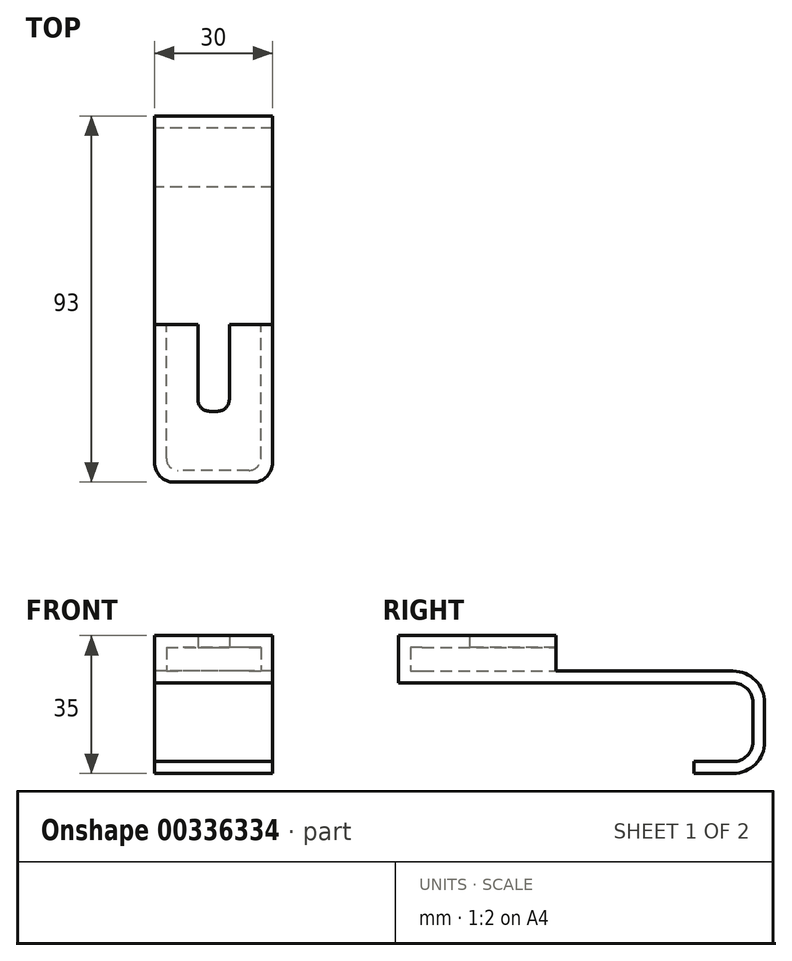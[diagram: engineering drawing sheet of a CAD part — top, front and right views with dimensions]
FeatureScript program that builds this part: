
annotation { "Feature Type Name" : "Feature", "Feature Type Description" : "" }
export const myFeature = defineFeature(function(context is Context, id is Id, definition is map)
    precondition{}
    {
        {
            var Q0;
            Q0=qCreatedBy(makeId("Top.planeOp"),FACE);
            var sketch = newSketch(context, id + "F0", { "sketchPlane" : qUnion([Q0])});
            skLineSegment(sketch, "E0.bottom", {"start": v(-5, 0) * mm, "end": v(-25, 0) * mm});
            skLineSegment(sketch, "E0.top", {"start": v(0, 40) * mm, "end": v(-30, 40) * mm});
            skLineSegment(sketch, "E0.left", {"start": v(0, 5) * mm, "end": v(0, 40) * mm});
            skLineSegment(sketch, "E0.right", {"start": v(-30, 5) * mm, "end": v(-30, 40) * mm});
            skPoint(sketch, "E1.visualSharp", {"position": v(-30, 0) * mm});
            skArc(sketch, "E1.filletArc", {"start": v(-30, 5) * mm, "mid": v(-28.54, 1.46) * mm, "end": v(-25, 0) * mm});
            skPoint(sketch, "E2.visualSharp", {"position": v(0, 0) * mm});
            skArc(sketch, "E2.filletArc", {"start": v(-5, 0) * mm, "mid": v(-1.46, 1.46) * mm, "end": v(0, 5) * mm});
            skSolve(sketch);
        }
        {
            var Q0;
            Q0=makeQuery(id+"F0.imprint","IMPRINT",FACE,{"disambiguationData":[TD([[makeQuery(id+"F0.imprint","IMPRINT",EDGE,{"derivedFrom":sQuery(id+"F0.wireOp",EDGE,"E0.bottom")}),-1.0]])]});
            extrude(context, id + "F1", {"entities" : qUnion([Q0]), "depth" : 3 * mm});
        }
        {
            var Q0;
            Q0=makeQuery(id+"F1.opExtrude","CAP_FACE",FACE,{"disambiguationData":[OSD([sQuery(id+"F0.wireOp",EDGE,"E0.bottom"),sQuery(id+"F0.wireOp",EDGE,"E0.top"),sQuery(id+"F0.wireOp",EDGE,"E0.left"),sQuery(id+"F0.wireOp",EDGE,"E0.right"),sQuery(id+"F0.wireOp",EDGE,"E1.filletArc"),sQuery(id+"F0.wireOp",EDGE,"E2.filletArc")])],"isStart":false});
            var sketch = newSketch(context, id + "F2", { "sketchPlane" : qUnion([Q0])});
            skLineSegment(sketch, "E3.0", {"start": v(-27, 6) * mm, "end": v(-27, 40) * mm});
            skLineSegment(sketch, "E3.1", {"start": v(-6, 3) * mm, "end": v(-24, 3) * mm});
            skLineSegment(sketch, "E3.2", {"start": v(-3, 6) * mm, "end": v(-3, 40) * mm});
            skPoint(sketch, "E4.visualSharp", {"position": v(-27, 3) * mm});
            skArc(sketch, "E4.filletArc", {"start": v(-27, 6) * mm, "mid": v(-26.12, 3.88) * mm, "end": v(-24, 3) * mm});
            skPoint(sketch, "E5.visualSharp", {"position": v(-3, 3) * mm});
            skArc(sketch, "E5.filletArc", {"start": v(-6, 3) * mm, "mid": v(-3.88, 3.88) * mm, "end": v(-3, 6) * mm});
            skSolve(sketch);
        }
        {
            var Q0;
            {var subQ2=sQuery(id+"F2.wireOp",EDGE,"E3.0");Q0=makeQuery(id+"F2.imprint","IMPRINT",FACE,{"disambiguationData":[TD([[makeQuery(id+"F2.imprint","IMPRINT",EDGE,{"derivedFrom":subQ2}),1.0]])]});}
            extrude(context, id + "F3", {"entities" : qUnion([Q0]), "operationType" : NewBodyOperationType.ADD, "depth" : 6 * mm});
        }
        {
            var Q0;
            Q0=makeQuery(id+"F3.opExtrude","CAP_FACE",FACE,{"disambiguationData":[OSD([sQuery(id+"F0.wireOp",EDGE,"E0.bottom"),sQuery(id+"F0.wireOp",EDGE,"E0.top"),sQuery(id+"F0.wireOp",EDGE,"E0.left"),sQuery(id+"F0.wireOp",EDGE,"E0.right"),sQuery(id+"F0.wireOp",EDGE,"E1.filletArc"),sQuery(id+"F0.wireOp",EDGE,"E2.filletArc"),sQuery(id+"F2.wireOp",EDGE,"E3.0"),sQuery(id+"F2.wireOp",EDGE,"E3.1"),sQuery(id+"F2.wireOp",EDGE,"E3.2"),sQuery(id+"F2.wireOp",EDGE,"E4.filletArc"),sQuery(id+"F2.wireOp",EDGE,"E5.filletArc")])],"isStart":false});
            var sketch = newSketch(context, id + "F4", { "sketchPlane" : qUnion([Q0])});
            skLineSegment(sketch, "E6.bottom", {"start": v(-5, 0) * mm, "end": v(-25, 0) * mm});
            skLineSegment(sketch, "E6.left", {"start": v(0, 5) * mm, "end": v(0, 40) * mm});
            skLineSegment(sketch, "E6.right", {"start": v(-30, 5) * mm, "end": v(-30, 40) * mm});
            skPoint(sketch, "E7.visualSharp", {"position": v(-30, 0) * mm});
            skArc(sketch, "E7.filletArc", {"start": v(-30, 5) * mm, "mid": v(-28.54, 1.46) * mm, "end": v(-25, 0) * mm});
            skPoint(sketch, "E8.visualSharp", {"position": v(0, 0) * mm});
            skArc(sketch, "E8.filletArc", {"start": v(-5, 0) * mm, "mid": v(-1.46, 1.46) * mm, "end": v(0, 5) * mm});
            skLineSegment(sketch, "E9", {"start": v(-30, 40) * mm, "end": v(-19, 40) * mm});
            skLineSegment(sketch, "E10", {"start": v(0, 40) * mm, "end": v(-11, 40) * mm});
            skLineSegment(sketch, "E11", {"start": v(-19, 40) * mm, "end": v(-19, 21) * mm});
            skLineSegment(sketch, "E12", {"start": v(-16, 18) * mm, "end": v(-14, 18) * mm});
            skLineSegment(sketch, "E13", {"start": v(-11, 21) * mm, "end": v(-11, 40) * mm});
            skPoint(sketch, "E14.visualSharp", {"position": v(-19, 18) * mm});
            skArc(sketch, "E14.filletArc", {"start": v(-19, 21) * mm, "mid": v(-18.12, 18.88) * mm, "end": v(-16, 18) * mm});
            skPoint(sketch, "E15.visualSharp", {"position": v(-11, 18) * mm});
            skArc(sketch, "E15.filletArc", {"start": v(-14, 18) * mm, "mid": v(-11.88, 18.88) * mm, "end": v(-11, 21) * mm});
            skSolve(sketch);
        }
        {
            var Q0;
            {var subQ4=sQuery(id+"F4.wireOp",EDGE,"E11");Q0=makeQuery(id+"F4.imprint","IMPRINT",FACE,{"disambiguationData":[TD([[makeQuery(id+"F4.imprint","IMPRINT",EDGE,{"derivedFrom":subQ4}),-1.0]])]});}
            var Q1;
            Q1=makeQuery(id+"F4.imprint","IMPRINT",FACE,{"disambiguationData":[TD([[makeQuery(id+"F4.imprint","IMPRINT",EDGE,{"derivedFrom":sQuery(id+"F4.wireOp",EDGE,"E6.bottom")}),-1.0]])]});
            extrude(context, id + "F5", {"entities" : qUnion([Q0, Q1]), "operationType" : NewBodyOperationType.ADD, "depth" : 3 * mm});
        }
        {
            var Q0;
            {var subQ0=sQuery(id+"F0.wireOp",EDGE,"E0.top");var subQ1=makeQuery(id+"F1.opExtrude","CAP_EDGE",EDGE,{"disambiguationData":[OSD([subQ0])],"isStart":false});Q0=makeQuery(id+"F5.boolean.opBoolean","MERGE",FACE,{"derivedFrom":[makeQuery(id+"F3.boolean.opBoolean","MERGE",FACE,{"derivedFrom":[makeQuery(id+"F1.opExtrude","SWEPT_FACE",FACE,{"disambiguationData":[OSD([subQ0])]}),makeQuery(id+"F3.opExtrude","SWEPT_FACE",FACE,{"disambiguationData":[OSD([subQ0]),TDD([makeQuery(id+"F2.imprint","IMPRINT",EDGE,{"disambiguationData":[TD([[makeQuery(id+"F2.imprint","INTERSECT",VERTEX,{"derivedFrom":[subQ1,makeQuery(id+"F1.opExtrude","CAP_EDGE",EDGE,{"disambiguationData":[OSD([sQuery(id+"F0.wireOp",EDGE,"E0.left")])],"isStart":false})]}),-1.0]])],"derivedFrom":subQ1})])]}),makeQuery(id+"F3.opExtrude","SWEPT_FACE",FACE,{"disambiguationData":[OSD([subQ0]),TDD([makeQuery(id+"F2.imprint","IMPRINT",EDGE,{"disambiguationData":[TD([[makeQuery(id+"F2.imprint","INTERSECT",VERTEX,{"derivedFrom":[subQ1,makeQuery(id+"F1.opExtrude","CAP_EDGE",EDGE,{"disambiguationData":[OSD([sQuery(id+"F0.wireOp",EDGE,"E0.right")])],"isStart":false})]}),1.0]])],"derivedFrom":subQ1})])]})]}),makeQuery(id+"F5.opExtrude","SWEPT_FACE",FACE,{"disambiguationData":[OSD([sQuery(id+"F4.wireOp",EDGE,"E9")])]}),makeQuery(id+"F5.opExtrude","SWEPT_FACE",FACE,{"disambiguationData":[OSD([sQuery(id+"F4.wireOp",EDGE,"E10")])]})]});}
            var sketch = newSketch(context, id + "F6", { "sketchPlane" : qUnion([Q0])});
            skLineSegment(sketch, "E16.bottom", {"start": v(30, 0) * mm, "end": v(0, 0) * mm});
            skLineSegment(sketch, "E16.top", {"start": v(30, 3) * mm, "end": v(0, 3) * mm});
            skLineSegment(sketch, "E16.left", {"start": v(30, 0) * mm, "end": v(30, 3) * mm});
            skLineSegment(sketch, "E16.right", {"start": v(0, 0) * mm, "end": v(0, 3) * mm});
            skSolve(sketch);
        }
        {
            var Q0;
            Q0=makeQuery(id+"F6.imprint","IMPRINT",FACE,{"disambiguationData":[TD([[makeQuery(id+"F6.imprint","IMPRINT",EDGE,{"derivedFrom":sQuery(id+"F6.wireOp",EDGE,"E16.bottom")}),1.0]])]});
            extrude(context, id + "F7", {"entities" : qUnion([Q0]), "operationType" : NewBodyOperationType.ADD, "depth" : 40 * mm});
        }
        {
            var Q0;
            {var subQ0=sQuery(id+"F0.wireOp",EDGE,"E0.right");Q0=makeQuery(id+"F7.boolean.opBoolean","MERGE",FACE,{"derivedFrom":[makeQuery(id+"F5.boolean.opBoolean","MERGE",FACE,{"derivedFrom":[makeQuery(id+"F3.boolean.opBoolean","MERGE",FACE,{"derivedFrom":[makeQuery(id+"F1.opExtrude","SWEPT_FACE",FACE,{"disambiguationData":[OSD([subQ0])]}),makeQuery(id+"F3.opExtrude","SWEPT_FACE",FACE,{"disambiguationData":[OSD([subQ0])]})]}),makeQuery(id+"F5.opExtrude","SWEPT_FACE",FACE,{"disambiguationData":[OSD([sQuery(id+"F4.wireOp",EDGE,"E6.right")])]})]}),makeQuery(id+"F7.opExtrude","SWEPT_FACE",FACE,{"disambiguationData":[OSD([sQuery(id+"F6.wireOp",EDGE,"E16.left")])]})]});}
            var sketch = newSketch(context, id + "F8", { "sketchPlane" : qUnion([Q0])});
            skLineSegment(sketch, "E17", {"start": v(-80, 0) * mm, "end": v(-85, 0) * mm});
            skLineSegment(sketch, "E18", {"start": v(-90, -5) * mm, "end": v(-90, -10) * mm});
            skPoint(sketch, "E19.visualSharp", {"position": v(-90, 0) * mm});
            skArc(sketch, "E19.filletArc", {"start": v(-85, 0) * mm, "mid": v(-88.54, -1.46) * mm, "end": v(-90, -5) * mm});
            skLineSegment(sketch, "E20.0", {"start": v(-93, -5) * mm, "end": v(-93, -10) * mm});
            skArc(sketch, "E20.1", {"start": v(-85, 3) * mm, "mid": v(-90.66, 0.66) * mm, "end": v(-93, -5) * mm});
            skLineSegment(sketch, "E21", {"start": v(-85, 3) * mm, "end": v(-80, 3) * mm});
            skLineSegment(sketch, "E22", {"start": v(-90, -10) * mm, "end": v(-90, -15) * mm});
            skLineSegment(sketch, "E23", {"start": v(-85, -20) * mm, "end": v(-80, -20) * mm});
            skPoint(sketch, "E24.visualSharp", {"position": v(-90, -20) * mm});
            skArc(sketch, "E24.filletArc", {"start": v(-90, -15) * mm, "mid": v(-88.54, -18.54) * mm, "end": v(-85, -20) * mm});
            skLineSegment(sketch, "E25.0", {"start": v(-85, -23) * mm, "end": v(-80, -23) * mm});
            skArc(sketch, "E25.1", {"start": v(-93, -15) * mm, "mid": v(-90.66, -20.66) * mm, "end": v(-85, -23) * mm});
            skLineSegment(sketch, "E25.2", {"start": v(-93, -10) * mm, "end": v(-93, -15) * mm});
            skLineSegment(sketch, "E26", {"start": v(-80, -20) * mm, "end": v(-75, -20) * mm});
            skLineSegment(sketch, "E27", {"start": v(-75, -20) * mm, "end": v(-75, -23) * mm});
            skLineSegment(sketch, "E28", {"start": v(-75, -23) * mm, "end": v(-80, -23) * mm});
            skSolve(sketch);
        }
        {
            var Q0;
            Q0=makeQuery(id+"F8.imprint","IMPRINT",FACE,{"disambiguationData":[TD([[makeQuery(id+"F8.imprint","IMPRINT",EDGE,{"derivedFrom":sQuery(id+"F8.wireOp",EDGE,"E17")}),-1.0]])]});
            extrude(context, id + "F9", {"entities" : qUnion([Q0]), "operationType" : NewBodyOperationType.ADD, "oppositeDirection" : true, "depth" : 30 * mm});
        }
    });
